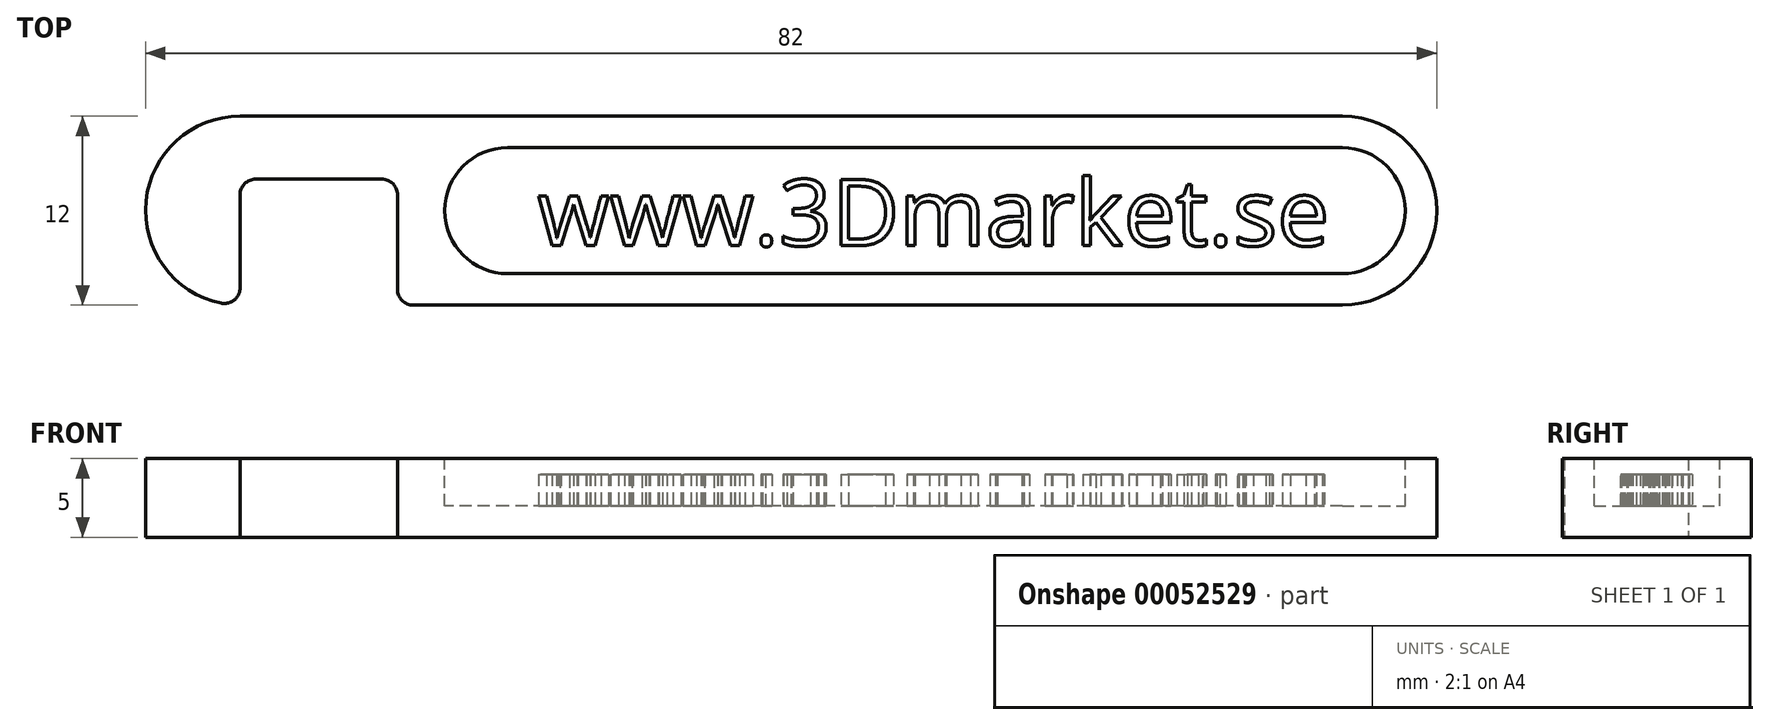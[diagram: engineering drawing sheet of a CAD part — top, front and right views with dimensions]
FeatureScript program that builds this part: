
annotation { "Feature Type Name" : "Feature", "Feature Type Description" : "" }
export const myFeature = defineFeature(function(context is Context, id is Id, definition is map)
    precondition{}
    {
        {
            var Q0;
            Q0=qCreatedBy(makeId("Top.planeOp"),FACE);
            var sketch = newSketch(context, id + "F0", { "sketchPlane" : qUnion([Q0])});
            skLineSegment(sketch, "E0.rect.bottom", {"start": v(35, 6) * mm, "end": v(-35, 6) * mm});
            skLineSegment(sketch, "E0.rect.top", {"start": v(35, -6) * mm, "end": v(-24, -6) * mm});
            skLineSegment(sketch, "E0.rect.left", {"start": v(41, 0) * mm, "end": v(41, 0) * mm});
            skLineSegment(sketch, "E0.rect.right", {"start": v(-41, 0) * mm, "end": v(-41, 0) * mm});
            skPoint(sketch, "E0.rect.middle", {"position": v(0, 0) * mm});
            skPoint(sketch, "E1.visualSharp", {"position": v(-41, 6) * mm});
            skArc(sketch, "E1.filletArc", {"start": v(-35, 6) * mm, "mid": v(-39.24, 4.24) * mm, "end": v(-41, 0) * mm});
            skPoint(sketch, "E2.visualSharp", {"position": v(-41, -6) * mm});
            skArc(sketch, "E2.filletArc", {"start": v(-41, 0) * mm, "mid": v(-39.65, -3.8) * mm, "end": v(-36.2, -5.88) * mm});
            skPoint(sketch, "E3.visualSharp", {"position": v(41, 6) * mm});
            skArc(sketch, "E3.filletArc", {"start": v(41, 0) * mm, "mid": v(39.24, 4.24) * mm, "end": v(35, 6) * mm});
            skPoint(sketch, "E4.visualSharp", {"position": v(41, -6) * mm});
            skArc(sketch, "E4.filletArc", {"start": v(35, -6) * mm, "mid": v(39.24, -4.24) * mm, "end": v(41, 0) * mm});
            skLineSegment(sketch, "E5", {"start": v(-35, -4.9) * mm, "end": v(-35, 1) * mm});
            skLineSegment(sketch, "E6", {"start": v(-34, 2) * mm, "end": v(-26, 2) * mm});
            skLineSegment(sketch, "E7", {"start": v(-25, 1) * mm, "end": v(-25, -5) * mm});
            skPoint(sketch, "E8.visualSharp", {"position": v(-25, -6) * mm});
            skArc(sketch, "E8.filletArc", {"start": v(-25, -5) * mm, "mid": v(-24.7, -5.7) * mm, "end": v(-24, -6) * mm});
            skPoint(sketch, "E9.visualSharp", {"position": v(-35, -6) * mm});
            skArc(sketch, "E9.filletArc", {"start": v(-36.2, -5.88) * mm, "mid": v(-35.37, -5.67) * mm, "end": v(-35, -4.9) * mm});
            skPoint(sketch, "E10.visualSharp", {"position": v(-35, 2) * mm});
            skArc(sketch, "E10.filletArc", {"start": v(-34, 2) * mm, "mid": v(-34.7, 1.7) * mm, "end": v(-35, 1) * mm});
            skPoint(sketch, "E11.visualSharp", {"position": v(-25, 2) * mm});
            skArc(sketch, "E11.filletArc", {"start": v(-25, 1) * mm, "mid": v(-25.3, 1.7) * mm, "end": v(-26, 2) * mm});
            skSolve(sketch);
        }
        {
            var Q0;
            Q0=makeQuery(id+"F0.imprint","IMPRINT",FACE,{"disambiguationData":[TD([[makeQuery(id+"F0.imprint","IMPRINT",EDGE,{"derivedFrom":sQuery(id+"F0.wireOp",EDGE,"E0.rect.bottom")}),1.0]])]});
            extrude(context, id + "F1", {"entities" : qUnion([Q0]), "depth" : 5 * mm});
        }
        {
            var Q0;
            Q0=makeQuery(id+"F1.opExtrude","CAP_FACE",FACE,{"disambiguationData":[OSD([sQuery(id+"F0.wireOp",EDGE,"E0.rect.bottom"),sQuery(id+"F0.wireOp",EDGE,"E0.rect.top"),sQuery(id+"F0.wireOp",EDGE,"E1.filletArc"),sQuery(id+"F0.wireOp",EDGE,"E2.filletArc"),sQuery(id+"F0.wireOp",EDGE,"E3.filletArc"),sQuery(id+"F0.wireOp",EDGE,"E4.filletArc"),sQuery(id+"F0.wireOp",EDGE,"E5"),sQuery(id+"F0.wireOp",EDGE,"E6"),sQuery(id+"F0.wireOp",EDGE,"E7"),sQuery(id+"F0.wireOp",EDGE,"E8.filletArc"),sQuery(id+"F0.wireOp",EDGE,"E9.filletArc"),sQuery(id+"F0.wireOp",EDGE,"E10.filletArc"),sQuery(id+"F0.wireOp",EDGE,"E11.filletArc")])],"isStart":false});
            var sketch = newSketch(context, id + "F2", { "sketchPlane" : qUnion([Q0])});
            skArc(sketch, "E12.0", {"start": v(35, -4) * mm, "mid": v(39, 0) * mm, "end": v(35, 4) * mm});
            skLineSegment(sketch, "E13", {"start": v(35, -4) * mm, "end": v(-18, -4) * mm});
            skLineSegment(sketch, "E14", {"start": v(-22, 0) * mm, "end": v(-22, 0) * mm});
            skLineSegment(sketch, "E15", {"start": v(-18, 4) * mm, "end": v(35, 4) * mm});
            skPoint(sketch, "E16.visualSharp", {"position": v(-22, -4) * mm});
            skArc(sketch, "E16.filletArc", {"start": v(-22, 0) * mm, "mid": v(-20.83, -2.83) * mm, "end": v(-18, -4) * mm});
            skPoint(sketch, "E17.visualSharp", {"position": v(-22, 4) * mm});
            skArc(sketch, "E17.filletArc", {"start": v(-18, 4) * mm, "mid": v(-20.83, 2.83) * mm, "end": v(-22, 0) * mm});
            skSolve(sketch);
        }
        {
            var Q0;
            Q0=makeQuery(id+"F2.imprint","IMPRINT",FACE,{"disambiguationData":[TD([[makeQuery(id+"F2.imprint","IMPRINT",EDGE,{"derivedFrom":sQuery(id+"F2.wireOp",EDGE,"E12.0")}),1.0]])]});
            extrude(context, id + "F3", {"entities" : qUnion([Q0]), "operationType" : NewBodyOperationType.REMOVE, "oppositeDirection" : true, "depth" : 3 * mm});
        }
        {
            var Q0;
            Q0=makeQuery(id+"F3.boolean.opBoolean","COPY",FACE,{"derivedFrom":makeQuery(id+"F3.opExtrude","CAP_FACE",FACE,{"disambiguationData":[OSD([sQuery(id+"F2.wireOp",EDGE,"E12.0"),sQuery(id+"F2.wireOp",EDGE,"E13"),sQuery(id+"F2.wireOp",EDGE,"E15"),sQuery(id+"F2.wireOp",EDGE,"E16.filletArc"),sQuery(id+"F2.wireOp",EDGE,"E17.filletArc")])],"isStart":false})});
            var sketch = newSketch(context, id + "F4", { "sketchPlane" : qUnion([Q0])});
            skText(sketch, "E18", { "text": "www.3Dmarket.se", "fontName": "OpenSans-Regular.ttf"});
            const initialGuessF4  = {"E18": [-0.0161, -0.00223, 1, 0, 0.00424]};
            skSetInitialGuess(sketch, initialGuessF4);
            skSolve(sketch);
        }
        {
            var Q0;
            Q0 = qSketchRegion(id + "F4", true);
            extrude(context, id + "F5", {"entities" : qUnion([Q0]), "operationType" : NewBodyOperationType.ADD, "depth" : 2 * mm});
        }
    });
